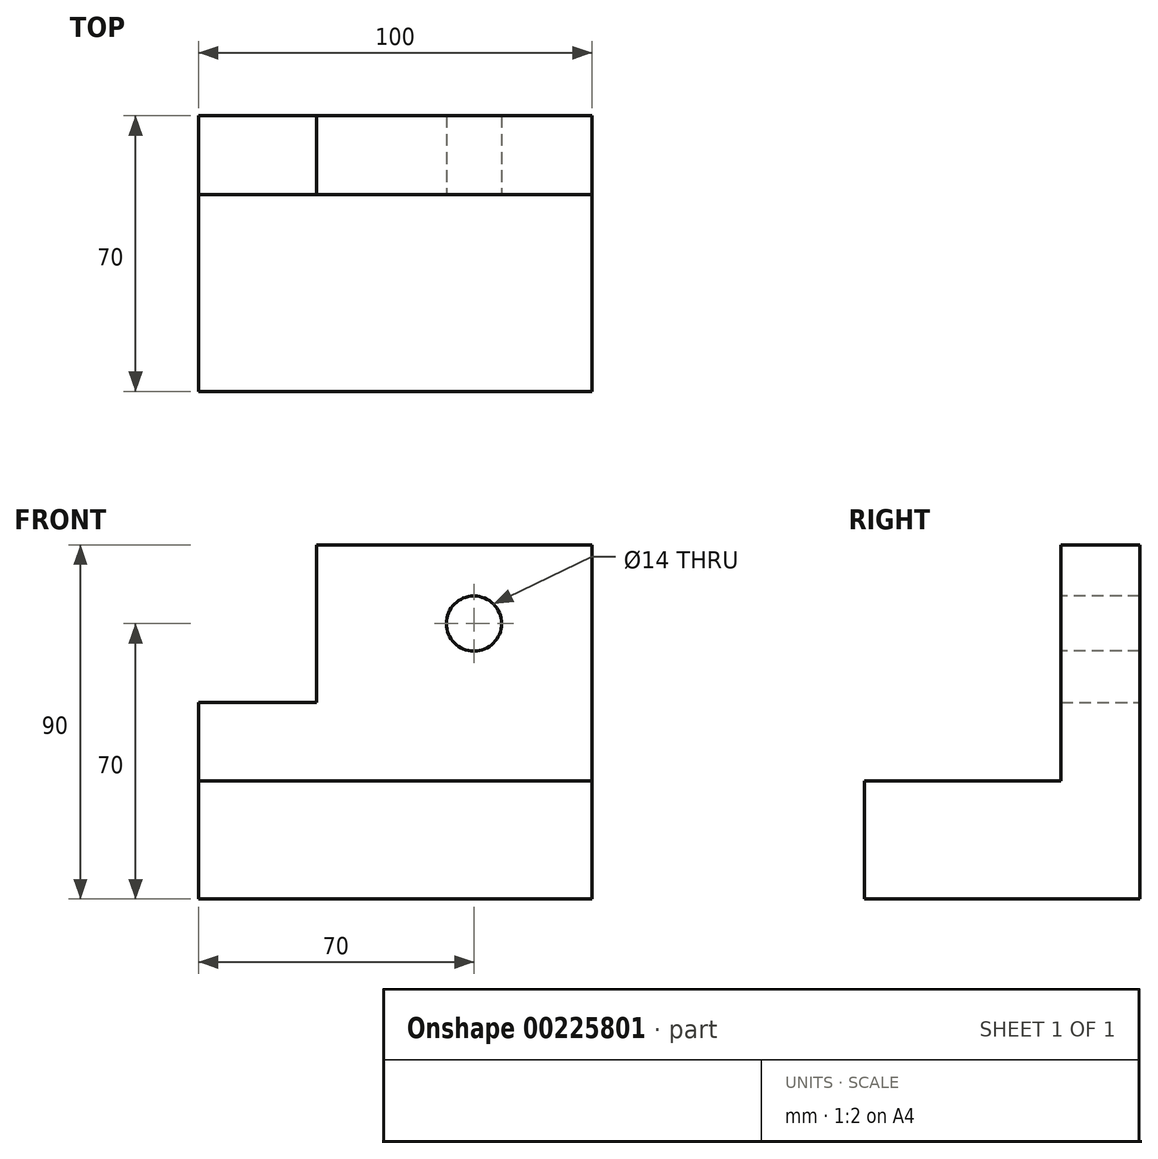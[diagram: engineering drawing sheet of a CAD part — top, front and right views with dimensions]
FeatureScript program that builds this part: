
annotation { "Feature Type Name" : "Feature", "Feature Type Description" : "" }
export const myFeature = defineFeature(function(context is Context, id is Id, definition is map)
    precondition{}
    {
        {
            var Q0;
            Q0=qCreatedBy(makeId("Front.planeOp"),FACE);
            var sketch = newSketch(context, id + "F0", { "sketchPlane" : qUnion([Q0])});
            skLineSegment(sketch, "E0.bottom", {"start": v(-70, 20) * mm, "end": v(30, 20) * mm});
            skLineSegment(sketch, "E0.top", {"start": v(-70, -70) * mm, "end": v(30, -70) * mm});
            skLineSegment(sketch, "E0.left", {"start": v(-70, 20) * mm, "end": v(-70, -70) * mm});
            skLineSegment(sketch, "E0.right", {"start": v(30, 20) * mm, "end": v(30, -70) * mm});
            skSolve(sketch);
        }
        {
            var Q0;
            Q0 = qSketchRegion(id + "F0", true);
            extrude(context, id + "F1", {"entities" : qUnion([Q0]), "depth" : 70 * mm});
        }
        {
            var Q0;
            Q0=makeQuery(id+"F1.opExtrude","SWEPT_FACE",FACE,{"disambiguationData":[OSD([sQuery(id+"F0.wireOp",EDGE,"E0.right")])]});
            var sketch = newSketch(context, id + "F2", { "sketchPlane" : qUnion([Q0])});
            skLineSegment(sketch, "E1.bottom", {"start": v(-80, 30) * mm, "end": v(-20, 30) * mm});
            skLineSegment(sketch, "E1.top", {"start": v(-80, -40) * mm, "end": v(-20, -40) * mm});
            skLineSegment(sketch, "E1.left", {"start": v(-80, 30) * mm, "end": v(-80, -40) * mm});
            skLineSegment(sketch, "E1.right", {"start": v(-20, 30) * mm, "end": v(-20, -40) * mm});
            skSolve(sketch);
        }
        {
            var Q0;
            Q0 = qSketchRegion(id + "F2", true);
            extrude(context, id + "F3", {"entities" : qUnion([Q0]), "operationType" : NewBodyOperationType.REMOVE, "endBound" : BoundingType.THROUGH_ALL, "oppositeDirection" : true, "depth" : 25 * mm});
        }
        {
            var Q0;
            Q0=makeQuery(id+"F3.boolean.opBoolean","COPY",FACE,{"derivedFrom":makeQuery(id+"F3.opExtrude","SWEPT_FACE",FACE,{"disambiguationData":[OSD([sQuery(id+"F2.wireOp",EDGE,"E1.right")])]})});
            var sketch = newSketch(context, id + "F4", { "sketchPlane" : qUnion([Q0])});
            skLineSegment(sketch, "E2.bottom", {"start": v(-80, 30) * mm, "end": v(-40, 30) * mm});
            skLineSegment(sketch, "E2.top", {"start": v(-80, -20) * mm, "end": v(-40, -20) * mm});
            skLineSegment(sketch, "E2.left", {"start": v(-80, 30) * mm, "end": v(-80, -20) * mm});
            skLineSegment(sketch, "E2.right", {"start": v(-40, 30) * mm, "end": v(-40, -20) * mm});
            skSolve(sketch);
        }
        {
            var Q0;
            Q0 = qSketchRegion(id + "F4", true);
            extrude(context, id + "F5", {"entities" : qUnion([Q0]), "operationType" : NewBodyOperationType.REMOVE, "endBound" : BoundingType.THROUGH_ALL, "oppositeDirection" : true, "depth" : 25 * mm});
        }
        {
            var Q0;
            Q0=makeQuery(id+"F3.boolean.opBoolean","COPY",FACE,{"derivedFrom":makeQuery(id+"F3.opExtrude","SWEPT_FACE",FACE,{"disambiguationData":[OSD([sQuery(id+"F2.wireOp",EDGE,"E1.right")])]})});
            var sketch = newSketch(context, id + "F6", { "sketchPlane" : qUnion([Q0])});
            skCircle(sketch, "E3", {"center": v(0, 0) * mm, "radius": 7 * mm});
            skSolve(sketch);
        }
        {
            var Q0;
            Q0 = qSketchRegion(id + "F6", true);
            extrude(context, id + "F7", {"entities" : qUnion([Q0]), "operationType" : NewBodyOperationType.REMOVE, "endBound" : BoundingType.THROUGH_ALL, "oppositeDirection" : true, "depth" : 25 * mm});
        }
    });
